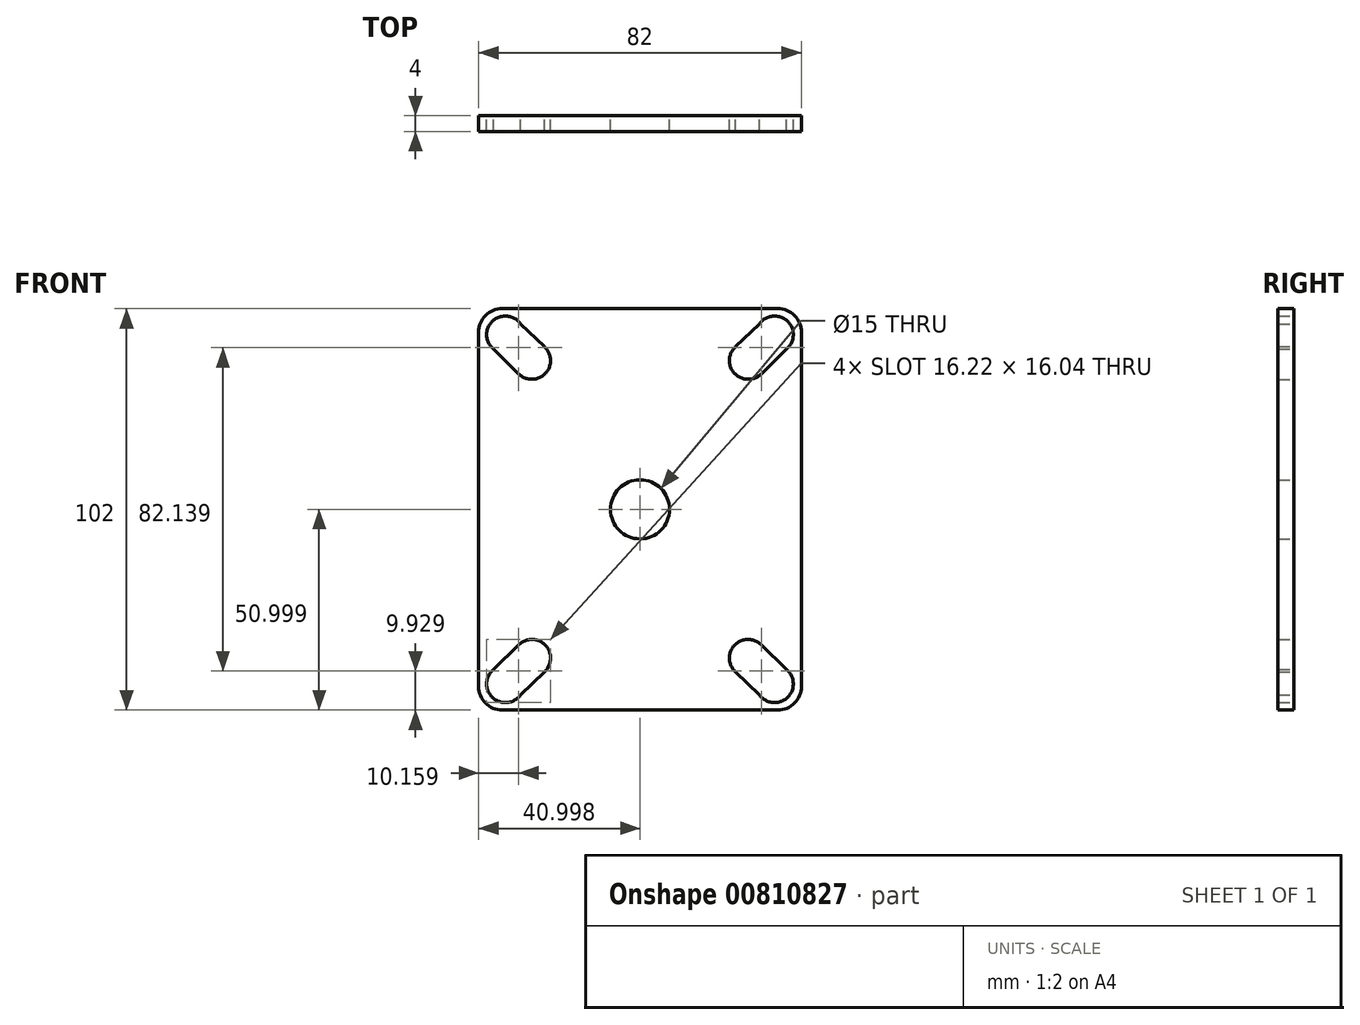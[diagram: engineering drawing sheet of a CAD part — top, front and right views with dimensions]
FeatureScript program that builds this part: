
annotation { "Feature Type Name" : "Feature", "Feature Type Description" : "" }
export const myFeature = defineFeature(function(context is Context, id is Id, definition is map)
    precondition{}
    {
        {
            var Q0;
            Q0=qCreatedBy(makeId("Front.planeOp"),FACE);
            var sketch = newSketch(context, id + "F0", { "sketchPlane" : qUnion([Q0])});
            skLineSegment(sketch, "E0.bottom", {"start": v(-49.64, 92.1) * mm, "end": v(32.36, 92.1) * mm});
            skLineSegment(sketch, "E0.top", {"start": v(-49.64, -9.9) * mm, "end": v(32.36, -9.9) * mm});
            skLineSegment(sketch, "E0.left", {"start": v(-49.64, 92.1) * mm, "end": v(-49.64, -9.9) * mm});
            skLineSegment(sketch, "E0.right", {"start": v(32.36, 92.1) * mm, "end": v(32.36, -9.9) * mm});
            skLineSegment(sketch, "E1", {"start": v(32.36, -9.9) * mm, "end": v(32.36, -1.9) * mm});
            skCircle(sketch, "E2", {"center": v(25.56, -3.26) * mm, "radius": 4.75 * mm});
            skLineSegment(sketch, "E3", {"start": v(32.36, 41.1) * mm, "end": v(-49.64, 41.1) * mm});
            skLineSegment(sketch, "E4", {"start": v(-8.64, 92.1) * mm, "end": v(-8.64, -9.9) * mm});
            skLineSegment(sketch, "E5", {"start": v(32.36, -9.9) * mm, "end": v(25.56, -3.26) * mm});
            skLineSegment(sketch, "E6", {"start": v(25.56, -3.26) * mm, "end": v(6.98, 14.88) * mm});
            skCircle(sketch, "E7", {"center": v(18.83, 3.3) * mm, "radius": 4.75 * mm});
            skLineSegment(sketch, "E8", {"start": v(22.13, 6.73) * mm, "end": v(29.16, -0.16) * mm});
            skLineSegment(sketch, "E9", {"start": v(15.43, 0) * mm, "end": v(22.97, -7.24) * mm});
            skCircle(sketch, "E10.MirrorC", {"center": v(-36.12, 3.3) * mm, "radius": 4.75 * mm});
            skCircle(sketch, "E11.MirrorC", {"center": v(-42.84, -3.26) * mm, "radius": 4.75 * mm});
            skLineSegment(sketch, "E12.MirrorCS", {"start": v(-32.7, 0) * mm, "end": v(-40.26, -7.24) * mm});
            skLineSegment(sketch, "E13.MirrorCS", {"start": v(-39.4, 6.73) * mm, "end": v(-46.44, -0.16) * mm});
            skLineSegment(sketch, "E14.MirrorCS", {"start": v(22.13, 75.48) * mm, "end": v(29.16, 82.37) * mm});
            skCircle(sketch, "E15.MirrorC", {"center": v(18.83, 78.9) * mm, "radius": 4.75 * mm});
            skLineSegment(sketch, "E16.MirrorCS", {"start": v(15.43, 82.22) * mm, "end": v(22.97, 89.46) * mm});
            skCircle(sketch, "E17.MirrorC", {"center": v(25.56, 85.47) * mm, "radius": 4.75 * mm});
            skCircle(sketch, "E18.MirrorC", {"center": v(-36.12, 78.9) * mm, "radius": 4.75 * mm});
            skLineSegment(sketch, "E19.MirrorCS", {"start": v(-39.4, 75.48) * mm, "end": v(-46.44, 82.37) * mm});
            skCircle(sketch, "E20.MirrorC", {"center": v(-42.84, 85.47) * mm, "radius": 4.75 * mm});
            skLineSegment(sketch, "E21.MirrorCS", {"start": v(-32.7, 82.22) * mm, "end": v(-40.26, 89.46) * mm});
            skCircle(sketch, "E22", {"center": v(-8.64, 41.1) * mm, "radius": 7.5 * mm});
            skSolve(sketch);
        }
        {
            var Q0;
            Q0 = qSketchRegion(id + "F0", true);
            extrude(context, id + "F1", {"entities" : qUnion([Q0]), "depth" : 4 * mm, "offsetDistance" : 25 * mm});
        }
        {
            var Q0;
            Q0=makeQuery(id+"F1.opExtrude","SWEPT_EDGE",EDGE,{"disambiguationData":[OSD([sQuery(id+"F0.wireOp",EDGE,"E0.bottom"),sQuery(id+"F0.wireOp",EDGE,"E0.left")])]});
            var Q1;
            Q1=makeQuery(id+"F1.opExtrude","SWEPT_EDGE",EDGE,{"disambiguationData":[OSD([sQuery(id+"F0.wireOp",EDGE,"E0.bottom"),sQuery(id+"F0.wireOp",EDGE,"E0.right")])]});
            var Q2;
            Q2=makeQuery(id+"F1.opExtrude","SWEPT_EDGE",EDGE,{"disambiguationData":[OSD([sQuery(id+"F0.wireOp",EDGE,"E0.top"),sQuery(id+"F0.wireOp",EDGE,"E1")])]});
            var Q3;
            Q3=makeQuery(id+"F1.opExtrude","SWEPT_EDGE",EDGE,{"disambiguationData":[OSD([sQuery(id+"F0.wireOp",EDGE,"E0.top"),sQuery(id+"F0.wireOp",EDGE,"E0.left")])]});
            fillet(context, id + "F2", {"entities" : qUnion([Q0, Q1, Q2, Q3]), "radius" : 6 * mm, "tangentPropagation" : true, "allowEdgeOverflow" : false});
        }
    });
